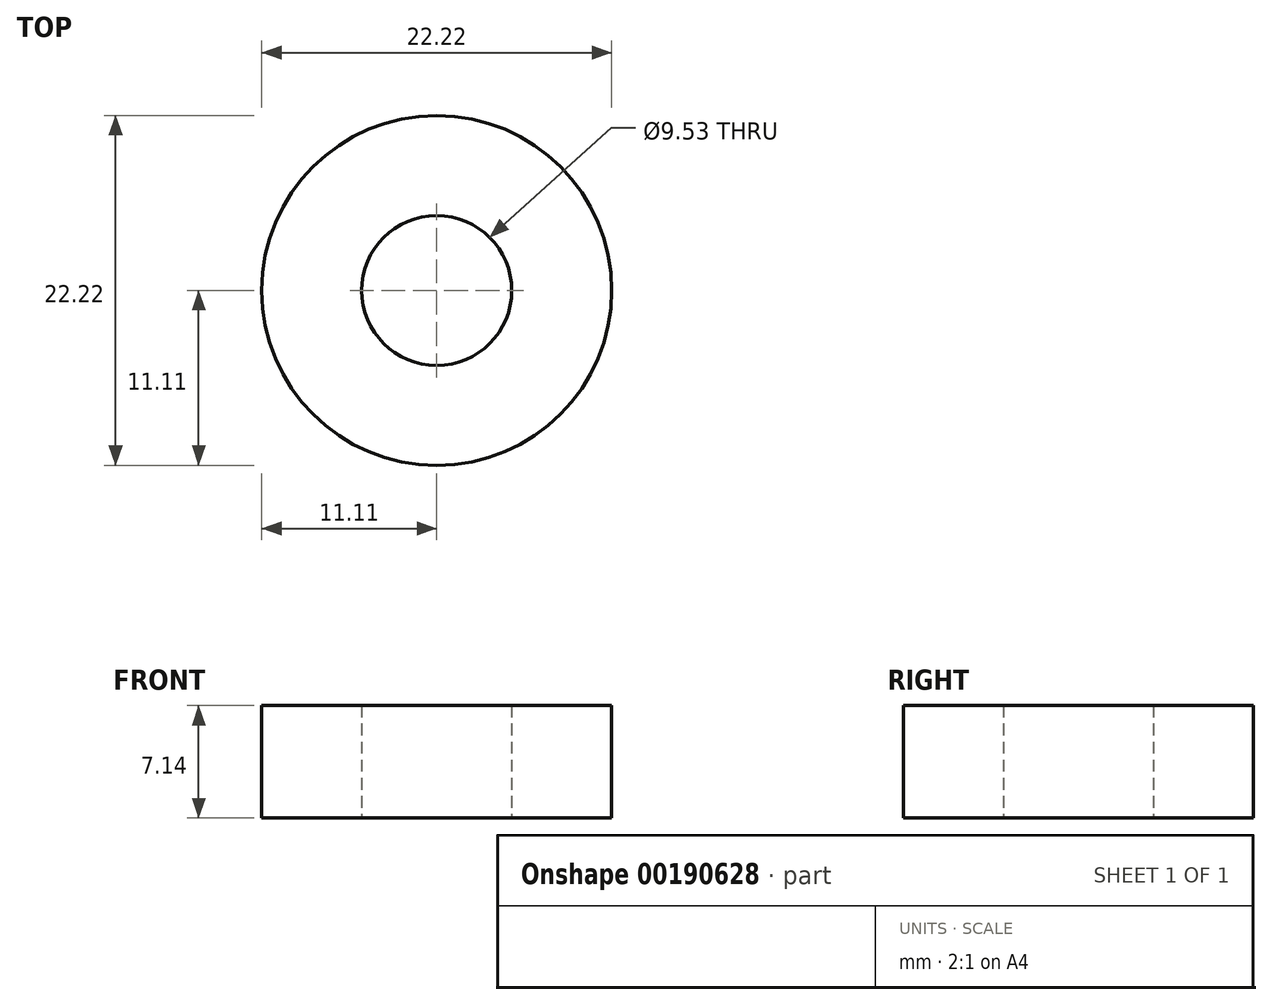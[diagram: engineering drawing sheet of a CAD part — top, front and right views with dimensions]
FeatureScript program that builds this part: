
annotation { "Feature Type Name" : "Feature", "Feature Type Description" : "" }
export const myFeature = defineFeature(function(context is Context, id is Id, definition is map)
    precondition{}
    {
        {
            var Q0;
            Q0=qCreatedBy(makeId("Top.planeOp"),FACE);
            var sketch = newSketch(context, id + "F0", { "sketchPlane" : qUnion([Q0])});
            skCircle(sketch, "E0", {"center": v(0, 0) * mm, "radius": 4.76 * mm});
            skCircle(sketch, "E1", {"center": v(0, 0) * mm, "radius": 11.11 * mm});
            skSolve(sketch);
        }
        {
            var Q0;
            Q0=makeQuery(id+"F0.imprint","IMPRINT",FACE,{"disambiguationData":[TD([[makeQuery(id+"F0.imprint","IMPRINT",EDGE,{"derivedFrom":sQuery(id+"F0.wireOp",EDGE,"E0")}),-1.0]])]});
            extrude(context, id + "F1", {"entities" : qUnion([Q0]), "depth" : 7.14 * mm});
        }
    });
